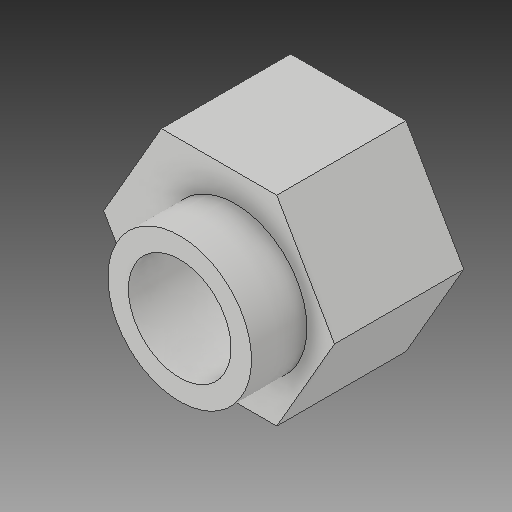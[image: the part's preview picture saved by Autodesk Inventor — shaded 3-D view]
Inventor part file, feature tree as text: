
AUTODESK INVENTOR PART (.ipt)
format: ipt  version: 2017 (Build 210142000, 142)  size: 120,832 bytes
history: native  units: mm
features: other x3, sketch x3
ambient origin geometry x8: Origin, YZ Plane, XZ Plane, XY Plane, X Axis, Y Axis, Z Axis, Center Point
bodies: Solid1 (feature_tree)
feature tree (6):
  other  "Eccentric Spacer_MIR1.ipt"
  other  "Solid1::Eccentric Spacer_MIR1.ipt"
  other  "TaggingFeature1"
  sketch  "Sketch1"  dims[d0=10.0mm]
  sketch  "Sketch2"
  sketch  "Sketch3"
